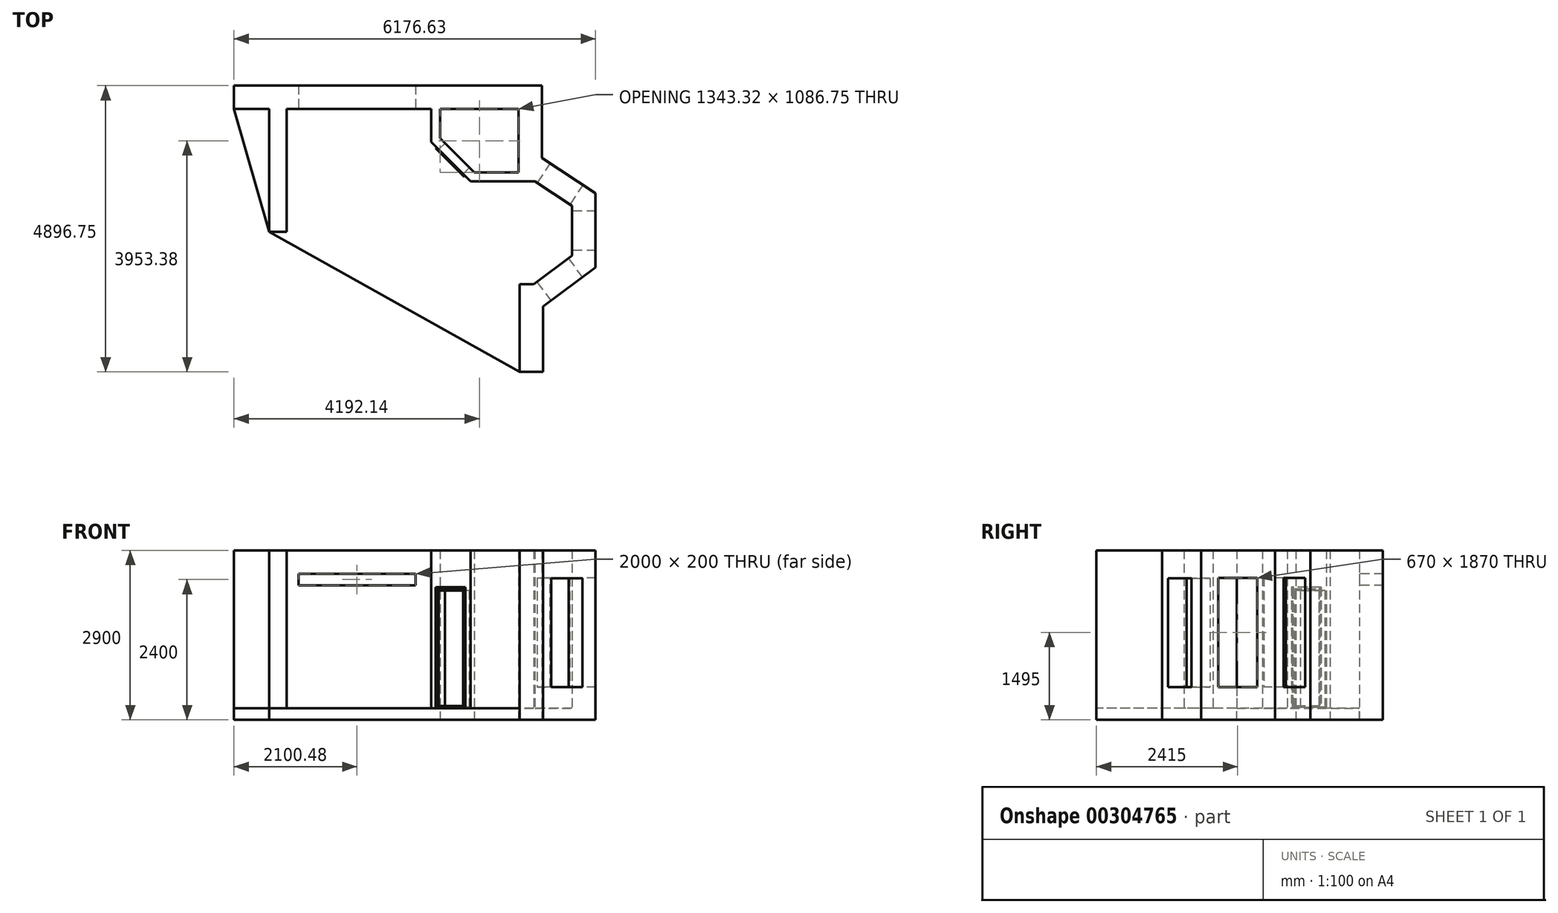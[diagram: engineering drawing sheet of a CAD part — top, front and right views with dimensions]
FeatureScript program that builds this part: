
annotation { "Feature Type Name" : "Feature", "Feature Type Description" : "" }
export const myFeature = defineFeature(function(context is Context, id is Id, definition is map)
    precondition{}
    {
        {
            var Q0;
            Q0=qCreatedBy(makeId("Top.planeOp"),FACE);
            var sketch = newSketch(context, id + "F0", { "sketchPlane" : qUnion([Q0])});
            skLineSegment(sketch, "E0", {"start": v(-112.53, -1087.53) * mm, "end": v(2357.47, -1087.53) * mm});
            skLineSegment(sketch, "E1", {"start": v(2357.47, -1087.53) * mm, "end": v(2357.47, -1652.53) * mm});
            skLineSegment(sketch, "E2", {"start": v(2357.47, -1652.53) * mm, "end": v(3029.22, -2324.28) * mm});
            skLineSegment(sketch, "E3", {"start": v(3029.22, -2324.28) * mm, "end": v(4130.22, -2324.28) * mm});
            skLineSegment(sketch, "E4", {"start": v(4130.22, -2324.28) * mm, "end": v(4763.62, -2744.28) * mm});
            skLineSegment(sketch, "E5", {"start": v(4763.62, -2744.28) * mm, "end": v(4763.62, -3594.28) * mm});
            skLineSegment(sketch, "E6", {"start": v(4763.62, -3594.28) * mm, "end": v(4106.13, -4084.28) * mm});
            skLineSegment(sketch, "E7", {"start": v(4106.13, -4084.28) * mm, "end": v(3866.13, -4084.28) * mm});
            skLineSegment(sketch, "E8", {"start": v(3866.13, -4084.28) * mm, "end": v(3866.13, -5584.28) * mm});
            skLineSegment(sketch, "E9", {"start": v(-112.53, -1087.53) * mm, "end": v(-112.53, -3187.53) * mm});
            skLineSegment(sketch, "E10", {"start": v(-112.53, -3187.53) * mm, "end": v(-412.53, -3187.53) * mm});
            skLineSegment(sketch, "E11", {"start": v(-412.53, -3187.53) * mm, "end": v(-412.53, -1087.53) * mm});
            skLineSegment(sketch, "E12", {"start": v(-412.53, -1087.53) * mm, "end": v(-1013, -1087.53) * mm});
            skLineSegment(sketch, "E13.0", {"start": v(4266.13, -4463.9) * mm, "end": v(4266.13, -5584.28) * mm});
            skLineSegment(sketch, "E13.1", {"start": v(5163.62, -3795.04) * mm, "end": v(4266.13, -4463.9) * mm});
            skLineSegment(sketch, "E13.2", {"start": v(5163.62, -2529.56) * mm, "end": v(5163.62, -3795.04) * mm});
            skLineSegment(sketch, "E13.3", {"start": v(4250.79, -1924.28) * mm, "end": v(5163.62, -2529.56) * mm});
            skLineSegment(sketch, "E13.4", {"start": v(-114.02, -687.53) * mm, "end": v(2757.47, -687.53) * mm});
            skLineSegment(sketch, "E13.5", {"start": v(2757.47, -687.53) * mm, "end": v(2757.47, -1486.84) * mm});
            skLineSegment(sketch, "E13.6", {"start": v(2757.47, -1486.84) * mm, "end": v(3194.9, -1924.28) * mm});
            skLineSegment(sketch, "E13.7", {"start": v(3194.9, -1924.28) * mm, "end": v(4250.79, -1924.28) * mm});
            skLineSegment(sketch, "E14", {"start": v(-1013, -1087.53) * mm, "end": v(-1013, -687.53) * mm});
            skLineSegment(sketch, "E15", {"start": v(-1013, -687.53) * mm, "end": v(-114.02, -687.53) * mm});
            skLineSegment(sketch, "E16", {"start": v(3866.13, -5584.28) * mm, "end": v(4266.13, -5584.28) * mm});
            skSolve(sketch);
        }
        {
            var Q0;
            Q0=makeQuery(id+"F0.imprint","IMPRINT",FACE,{"disambiguationData":[TD([[makeQuery(id+"F0.imprint","IMPRINT",EDGE,{"derivedFrom":sQuery(id+"F0.wireOp",EDGE,"E0")}),1.0]])]});
            extrude(context, id + "F1", {"entities" : qUnion([Q0]), "depth" : 2700 * mm});
        }
        {
            var Q0;
            Q0=qCreatedBy(makeId("Top.planeOp"),FACE);
            var sketch = newSketch(context, id + "F2", { "sketchPlane" : qUnion([Q0])});
            skPoint(sketch, "E17.0", {"position": v(3866.13, -4084.28) * mm});
            skLineSegment(sketch, "E18.0", {"start": v(3850.79, -1924.28) * mm, "end": v(4250.79, -1924.28) * mm});
            skLineSegment(sketch, "E19.0", {"start": v(2757.47, -687.53) * mm, "end": v(2757.47, -1087.53) * mm});
            skPoint(sketch, "E20.0", {"position": v(2357.47, -1087.53) * mm});
            skLineSegment(sketch, "E21", {"start": v(2757.47, -1087.53) * mm, "end": v(3850.79, -1087.53) * mm});
            skPoint(sketch, "E22.0", {"position": v(4266.13, -4463.9) * mm});
            skLineSegment(sketch, "E23", {"start": v(2757.47, -687.53) * mm, "end": v(4250.79, -687.53) * mm});
            skLineSegment(sketch, "E24", {"start": v(4250.79, -1924.28) * mm, "end": v(4250.79, -687.53) * mm});
            skLineSegment(sketch, "E25", {"start": v(3850.79, -1087.53) * mm, "end": v(3850.79, -1924.28) * mm});
            skPoint(sketch, "E26.orphan", {"position": v(3194.9, -1924.28) * mm});
            skPoint(sketch, "E27.orphan", {"position": v(2757.47, -1486.84) * mm});
            skSolve(sketch);
        }
        {
            var Q0;
            Q0=makeQuery(id+"F2.imprint","IMPRINT",FACE,{"disambiguationData":[TD([[makeQuery(id+"F2.imprint","IMPRINT",EDGE,{"derivedFrom":sQuery(id+"F2.wireOp",EDGE,"E18.0")}),1.0]])]});
            extrude(context, id + "F3", {"entities" : qUnion([Q0]), "operationType" : NewBodyOperationType.ADD, "depth" : 2700 * mm});
        }
        {
            var Q0;
            Q0=qCreatedBy(makeId("Top.planeOp"),FACE);
            var sketch = newSketch(context, id + "F4", { "sketchPlane" : qUnion([Q0])});
            skLineSegment(sketch, "E28.0", {"start": v(2757.47, -1087.53) * mm, "end": v(2757.47, -1486.84) * mm});
            skLineSegment(sketch, "E29.0", {"start": v(2757.47, -1486.84) * mm, "end": v(3194.9, -1924.28) * mm});
            skLineSegment(sketch, "E30.0", {"start": v(3194.9, -1924.28) * mm, "end": v(3850.79, -1924.28) * mm});
            skLineSegment(sketch, "E31", {"start": v(2757.47, -1087.53) * mm, "end": v(2507.47, -1087.53) * mm});
            skLineSegment(sketch, "E32", {"start": v(2507.47, -1087.53) * mm, "end": v(2507.47, -1590.4) * mm});
            skLineSegment(sketch, "E33", {"start": v(2507.47, -1590.4) * mm, "end": v(3091.35, -2174.28) * mm});
            skLineSegment(sketch, "E34", {"start": v(3091.35, -2174.28) * mm, "end": v(3850.79, -2174.28) * mm});
            skLineSegment(sketch, "E35", {"start": v(3850.79, -2174.28) * mm, "end": v(3850.79, -1924.28) * mm});
            skSolve(sketch);
        }
        {
            var Q0;
            Q0=makeQuery(id+"F4.imprint","IMPRINT",FACE,{"disambiguationData":[TD([[makeQuery(id+"F4.imprint","IMPRINT",EDGE,{"derivedFrom":sQuery(id+"F4.wireOp",EDGE,"E28.0")}),-1.0]])]});
            extrude(context, id + "F5", {"entities" : qUnion([Q0]), "operationType" : NewBodyOperationType.REMOVE, "depth" : 2700 * mm});
        }
        {
            var Q0;
            Q0=makeQuery(id+"F3.boolean.opBoolean","MERGE",FACE,{"derivedFrom":[makeQuery(id+"F1.opExtrude","CAP_FACE",FACE,{"disambiguationData":[OSD([sQuery(id+"F0.wireOp",EDGE,"E0"),sQuery(id+"F0.wireOp",EDGE,"E1"),sQuery(id+"F0.wireOp",EDGE,"E2"),sQuery(id+"F0.wireOp",EDGE,"E3"),sQuery(id+"F0.wireOp",EDGE,"E4"),sQuery(id+"F0.wireOp",EDGE,"E5"),sQuery(id+"F0.wireOp",EDGE,"E6"),sQuery(id+"F0.wireOp",EDGE,"E7"),sQuery(id+"F0.wireOp",EDGE,"E8"),sQuery(id+"F0.wireOp",EDGE,"E9"),sQuery(id+"F0.wireOp",EDGE,"E10"),sQuery(id+"F0.wireOp",EDGE,"E11"),sQuery(id+"F0.wireOp",EDGE,"E12"),sQuery(id+"F0.wireOp",EDGE,"E13.0"),sQuery(id+"F0.wireOp",EDGE,"E13.1"),sQuery(id+"F0.wireOp",EDGE,"E13.2"),sQuery(id+"F0.wireOp",EDGE,"E13.3"),sQuery(id+"F0.wireOp",EDGE,"E13.4"),sQuery(id+"F0.wireOp",EDGE,"E13.5"),sQuery(id+"F0.wireOp",EDGE,"E13.6"),sQuery(id+"F0.wireOp",EDGE,"E13.7"),sQuery(id+"F0.wireOp",EDGE,"E14"),sQuery(id+"F0.wireOp",EDGE,"E15"),sQuery(id+"F0.wireOp",EDGE,"E16")])],"isStart":true}),makeQuery(id+"F3.opExtrude","CAP_FACE",FACE,{"disambiguationData":[OSD([sQuery(id+"F2.wireOp",EDGE,"E18.0"),sQuery(id+"F2.wireOp",EDGE,"E19.0"),sQuery(id+"F2.wireOp",EDGE,"E21"),sQuery(id+"F2.wireOp",EDGE,"E23"),sQuery(id+"F2.wireOp",EDGE,"E24"),sQuery(id+"F2.wireOp",EDGE,"E25")])],"isStart":true})]});
            var sketch = newSketch(context, id + "F6", { "sketchPlane" : qUnion([Q0])});
            skLineSegment(sketch, "E36.0", {"start": v(-1013, 687.53) * mm, "end": v(4250.79, 687.53) * mm});
            skPoint(sketch, "E37.0", {"position": v(4250.79, 1305.9) * mm});
            skLineSegment(sketch, "E38.0", {"start": v(4250.79, 1924.28) * mm, "end": v(4250.79, 687.53) * mm});
            skLineSegment(sketch, "E39.0", {"start": v(4250.79, 1924.28) * mm, "end": v(5163.62, 2529.56) * mm});
            skPoint(sketch, "E40.0", {"position": v(5163.62, 3162.3) * mm});
            skLineSegment(sketch, "E41.0", {"start": v(5163.62, 2529.56) * mm, "end": v(5163.62, 3795.04) * mm});
            skLineSegment(sketch, "E42.0", {"start": v(5163.62, 3795.04) * mm, "end": v(4266.13, 4463.9) * mm});
            skLineSegment(sketch, "E43.0", {"start": v(4266.13, 4463.9) * mm, "end": v(4266.13, 5584.28) * mm});
            skLineSegment(sketch, "E44.0", {"start": v(-1013, 1087.53) * mm, "end": v(-1013, 687.53) * mm});
            skPoint(sketch, "E45.0", {"position": v(-412.53, 3187.53) * mm});
            skLineSegment(sketch, "E46.0", {"start": v(3866.13, 5584.28) * mm, "end": v(4266.13, 5584.28) * mm});
            skLineSegment(sketch, "E47", {"start": v(-1013, 1087.53) * mm, "end": v(-412.53, 3187.53) * mm});
            skLineSegment(sketch, "E48", {"start": v(-412.53, 3187.53) * mm, "end": v(3866.13, 5584.28) * mm});
            skSolve(sketch);
        }
        {
            var Q0;
            Q0=makeQuery(id+"F6.imprint","IMPRINT",FACE,{"disambiguationData":[TD([[makeQuery(id+"F6.imprint","IMPRINT",EDGE,{"derivedFrom":sQuery(id+"F6.wireOp",EDGE,"E36.0")}),1.0]])]});
            var Q1;
            Q1=makeQuery(id+"F6.imprint","IMPRINT",FACE,{"disambiguationData":[TD([[makeQuery(id+"F6.imprint","IMPRINT",EDGE,{"derivedFrom":sQuery(id+"F6.wireOp",EDGE,"E47")}),-1.0]])]});
            var Q2;
            Q2=makeQuery(id+"F6.imprint","IMPRINT",FACE,{"disambiguationData":[TD([[makeQuery(id+"F6.imprint","IMPRINT",EDGE,{"derivedFrom":sQuery(id+"F6.wireOp",EDGE,"E48")}),-1.0]])]});
            var Q3;
            Q3=makeQuery(id+"F6.imprint","IMPRINT",FACE,{"disambiguationData":[TD([[makeQuery(id+"F6.imprint","IMPRINT",EDGE,{"derivedFrom":makeQuery(id+"F5.boolean.opBoolean","COPY",EDGE,{"derivedFrom":makeQuery(id+"F5.opExtrude","CAP_EDGE",EDGE,{"disambiguationData":[OSD([sQuery(id+"F4.wireOp",EDGE,"E32")])],"isStart":true})})}),-1.0]])]});
            extrude(context, id + "F7", {"entities" : qUnion([Q0, Q1, Q2, Q3]), "operationType" : NewBodyOperationType.ADD, "depth" : 200 * mm});
        }
        {
            var Q0;
            Q0=makeQuery(id+"F1.opExtrude","SWEPT_FACE",FACE,{"disambiguationData":[OSD([sQuery(id+"F0.wireOp",EDGE,"E2")])]});
            var sketch = newSketch(context, id + "F8", { "sketchPlane" : qUnion([Q0])});
            skLineSegment(sketch, "E49.bottom", {"start": v(2965.5, 2070) * mm, "end": v(3655.5, 2070) * mm});
            skLineSegment(sketch, "E49.top", {"start": v(2965.5, 10) * mm, "end": v(3655.5, 10) * mm});
            skLineSegment(sketch, "E49.left", {"start": v(2965.5, 2070) * mm, "end": v(2965.5, 10) * mm});
            skLineSegment(sketch, "E49.right", {"start": v(3655.5, 2070) * mm, "end": v(3655.5, 10) * mm});
            skSolve(sketch);
        }
        {
            var Q0;
            Q0=makeQuery(id+"F8.imprint","IMPRINT",FACE,{"disambiguationData":[TD([[makeQuery(id+"F8.imprint","IMPRINT",EDGE,{"derivedFrom":sQuery(id+"F8.wireOp",EDGE,"E49.bottom")}),-1.0]])]});
            extrude(context, id + "F9", {"entities" : qUnion([Q0]), "operationType" : NewBodyOperationType.ADD, "depth" : 25 * mm});
        }
        {
            var Q0;
            Q0=makeQuery(id+"F1.opExtrude","SWEPT_FACE",FACE,{"disambiguationData":[OSD([sQuery(id+"F0.wireOp",EDGE,"E4")])]});
            var sketch = newSketch(context, id + "F10", { "sketchPlane" : qUnion([Q0])});
            skLineSegment(sketch, "E50.bottom", {"start": v(4771.7, 2230) * mm, "end": v(5441.7, 2230) * mm});
            skLineSegment(sketch, "E50.top", {"start": v(4771.7, 360) * mm, "end": v(5441.7, 360) * mm});
            skLineSegment(sketch, "E50.left", {"start": v(4771.7, 2230) * mm, "end": v(4771.7, 360) * mm});
            skLineSegment(sketch, "E50.right", {"start": v(5441.7, 2230) * mm, "end": v(5441.7, 360) * mm});
            skPoint(sketch, "E51.0", {"position": v(5106.7, 2700) * mm});
            skSolve(sketch);
        }
        {
            var Q0;
            Q0=makeQuery(id+"F10.imprint","IMPRINT",FACE,{"disambiguationData":[TD([[makeQuery(id+"F10.imprint","IMPRINT",EDGE,{"derivedFrom":sQuery(id+"F10.wireOp",EDGE,"E50.bottom")}),-1.0]])]});
            extrude(context, id + "F11", {"entities" : qUnion([Q0]), "operationType" : NewBodyOperationType.REMOVE, "oppositeDirection" : true, "depth" : 500 * mm});
        }
        {
            var Q0;
            Q0=makeQuery(id+"F1.opExtrude","SWEPT_FACE",FACE,{"disambiguationData":[OSD([sQuery(id+"F0.wireOp",EDGE,"E5")])]});
            var sketch = newSketch(context, id + "F12", { "sketchPlane" : qUnion([Q0])});
            skLineSegment(sketch, "E52.bottom", {"start": v(2834.28, 2230) * mm, "end": v(3504.28, 2230) * mm});
            skLineSegment(sketch, "E52.top", {"start": v(2834.28, 360) * mm, "end": v(3504.28, 360) * mm});
            skLineSegment(sketch, "E52.left", {"start": v(2834.28, 2230) * mm, "end": v(2834.28, 360) * mm});
            skLineSegment(sketch, "E52.right", {"start": v(3504.28, 2230) * mm, "end": v(3504.28, 360) * mm});
            skPoint(sketch, "E53.0", {"position": v(3169.28, 2700) * mm});
            skSolve(sketch);
        }
        {
            var Q0;
            Q0=makeQuery(id+"F12.imprint","IMPRINT",FACE,{"disambiguationData":[TD([[makeQuery(id+"F12.imprint","IMPRINT",EDGE,{"derivedFrom":sQuery(id+"F12.wireOp",EDGE,"E52.bottom")}),-1.0]])]});
            extrude(context, id + "F13", {"entities" : qUnion([Q0]), "operationType" : NewBodyOperationType.REMOVE, "oppositeDirection" : true, "depth" : 500 * mm});
        }
        {
            var Q0;
            Q0=makeQuery(id+"F1.opExtrude","SWEPT_FACE",FACE,{"disambiguationData":[OSD([sQuery(id+"F0.wireOp",EDGE,"E6")])]});
            var sketch = newSketch(context, id + "F14", { "sketchPlane" : qUnion([Q0])});
            skLineSegment(sketch, "E54.bottom", {"start": v(-1596.79, 2220) * mm, "end": v(-926.79, 2220) * mm});
            skLineSegment(sketch, "E54.top", {"start": v(-1596.79, 360) * mm, "end": v(-926.79, 360) * mm});
            skLineSegment(sketch, "E54.left", {"start": v(-1596.79, 2220) * mm, "end": v(-1596.79, 360) * mm});
            skLineSegment(sketch, "E54.right", {"start": v(-926.79, 2220) * mm, "end": v(-926.79, 360) * mm});
            skPoint(sketch, "E55.0", {"position": v(-1261.79, 2700) * mm});
            skSolve(sketch);
        }
        {
            var Q0;
            Q0 = qSketchRegion(id + "F14", true);
            extrude(context, id + "F15", {"entities" : qUnion([Q0]), "operationType" : NewBodyOperationType.REMOVE, "oppositeDirection" : true, "depth" : 500 * mm});
        }
        {
            var Q0;
            Q0=makeQuery(id+"F1.opExtrude","SWEPT_FACE",FACE,{"disambiguationData":[OSD([sQuery(id+"F0.wireOp",EDGE,"E0")])]});
            var sketch = newSketch(context, id + "F16", { "sketchPlane" : qUnion([Q0])});
            skLineSegment(sketch, "E56.bottom", {"start": v(87.47, 2300) * mm, "end": v(2087.47, 2300) * mm});
            skLineSegment(sketch, "E56.top", {"start": v(87.47, 2100) * mm, "end": v(2087.47, 2100) * mm});
            skLineSegment(sketch, "E56.left", {"start": v(87.47, 2300) * mm, "end": v(87.47, 2100) * mm});
            skLineSegment(sketch, "E56.right", {"start": v(2087.47, 2300) * mm, "end": v(2087.47, 2100) * mm});
            skSolve(sketch);
        }
        {
            var Q0;
            Q0=makeQuery(id+"F16.imprint","IMPRINT",FACE,{"disambiguationData":[TD([[makeQuery(id+"F16.imprint","IMPRINT",EDGE,{"derivedFrom":sQuery(id+"F16.wireOp",EDGE,"E56.bottom")}),-1.0]])]});
            extrude(context, id + "F17", {"entities" : qUnion([Q0]), "operationType" : NewBodyOperationType.REMOVE, "oppositeDirection" : true, "depth" : 500 * mm});
        }
        {
            var Q0;
            {var subQ0=sQuery(id+"F6.wireOp",EDGE,"E46.0");var subQ1=sQuery(id+"F6.wireOp",EDGE,"E48");var subQ2=sQuery(id+"F6.wireOp",EDGE,"E47");var subQ3=makeQuery(id+"F7.opExtrude","CAP_FACE",FACE,{"disambiguationData":[OSD([sQuery(id+"F6.wireOp",EDGE,"E36.0"),sQuery(id+"F6.wireOp",EDGE,"E38.0"),sQuery(id+"F6.wireOp",EDGE,"E39.0"),sQuery(id+"F6.wireOp",EDGE,"E41.0"),sQuery(id+"F6.wireOp",EDGE,"E42.0"),sQuery(id+"F6.wireOp",EDGE,"E43.0"),sQuery(id+"F6.wireOp",EDGE,"E44.0"),subQ0,subQ2,subQ1])],"isStart":true});Q0=makeQuery(id+"F7.boolean.opBoolean","SPLIT",FACE,{"disambiguationData":[TD([makeQuery(id+"F1.opExtrude","SWEPT_FACE",FACE,{"disambiguationData":[OSD([sQuery(id+"F0.wireOp",EDGE,"E0")])]})])],"derivedFrom":subQ3});}
            var sketch = newSketch(context, id + "F18", { "sketchPlane" : qUnion([Q0])});
            skPoint(sketch, "E57.0", {"position": v(-112.53, -1087.53) * mm});
            skLineSegment(sketch, "E58.0", {"start": v(-112.53, -1087.53) * mm, "end": v(-112.53, -3187.53) * mm});
            skLineSegment(sketch, "E59.0", {"start": v(-112.53, -1087.53) * mm, "end": v(2357.47, -1087.53) * mm});
            skLineSegment(sketch, "E60", {"start": v(-112.53, -3187.53) * mm, "end": v(487.47, -3187.53) * mm});
            skLineSegment(sketch, "E61", {"start": v(487.47, -3187.53) * mm, "end": v(487.47, -2111.8) * mm});
            skLineSegment(sketch, "E62", {"start": v(487.47, -2111.8) * mm, "end": v(911.73, -1687.53) * mm});
            skLineSegment(sketch, "E63", {"start": v(911.73, -1687.53) * mm, "end": v(1797.47, -1687.53) * mm});
            skLineSegment(sketch, "E64", {"start": v(1797.47, -1687.53) * mm, "end": v(1797.47, -1087.53) * mm});
            skSolve(sketch);
        }
        {
            var Q0;
            Q0=makeQuery(id+"F8.imprint","IMPRINT",FACE,{"disambiguationData":[TD([[makeQuery(id+"F8.imprint","IMPRINT",EDGE,{"derivedFrom":sQuery(id+"F8.wireOp",EDGE,"E49.bottom")}),-1.0]])]});
            var sketch = newSketch(context, id + "F19", { "sketchPlane" : qUnion([Q0])});
            skLineSegment(sketch, "E65.bottom", {"start": v(3015.5, 2010) * mm, "end": v(3605.5, 2010) * mm});
            skLineSegment(sketch, "E65.top", {"start": v(3015.5, 20) * mm, "end": v(3605.5, 20) * mm});
            skLineSegment(sketch, "E65.left", {"start": v(3015.5, 2010) * mm, "end": v(3015.5, 20) * mm});
            skLineSegment(sketch, "E65.right", {"start": v(3605.5, 2010) * mm, "end": v(3605.5, 20) * mm});
            skPoint(sketch, "E65.middle", {"position": v(3310.5, 1015) * mm});
            skSolve(sketch);
        }
        {
            var Q0;
            Q0=makeQuery(id+"F19.imprint","IMPRINT",FACE,{"disambiguationData":[TD([[makeQuery(id+"F19.imprint","IMPRINT",EDGE,{"derivedFrom":sQuery(id+"F19.wireOp",EDGE,"E65.bottom")}),-1.0]])]});
            extrude(context, id + "F20", {"entities" : qUnion([Q0]), "operationType" : NewBodyOperationType.REMOVE, "oppositeDirection" : true, "depth" : 300 * mm});
        }
        {
            var Q0;
            Q0=makeQuery(id+"F9.opExtrude","CAP_FACE",FACE,{"disambiguationData":[OSD([sQuery(id+"F8.wireOp",EDGE,"E49.bottom"),sQuery(id+"F8.wireOp",EDGE,"E49.top"),sQuery(id+"F8.wireOp",EDGE,"E49.left"),sQuery(id+"F8.wireOp",EDGE,"E49.right")])],"isStart":false});
            var sketch = newSketch(context, id + "F21", { "sketchPlane" : qUnion([Q0])});
            skLineSegment(sketch, "E66.0.0", {"start": v(2965.5, 2070) * mm, "end": v(2965.5, 10) * mm});
            skLineSegment(sketch, "E66.0.1", {"start": v(2965.5, 10) * mm, "end": v(3655.5, 10) * mm});
            skLineSegment(sketch, "E66.0.2", {"start": v(3655.5, 10) * mm, "end": v(3655.5, 2070) * mm});
            skLineSegment(sketch, "E66.0.3", {"start": v(3655.5, 2070) * mm, "end": v(2965.5, 2070) * mm});
            skLineSegment(sketch, "E67.0", {"start": v(2990.5, 2045) * mm, "end": v(2990.5, 35) * mm});
            skLineSegment(sketch, "E67.1", {"start": v(3630.5, 2045) * mm, "end": v(2990.5, 2045) * mm});
            skLineSegment(sketch, "E67.2", {"start": v(3630.5, 35) * mm, "end": v(3630.5, 2045) * mm});
            skLineSegment(sketch, "E67.3", {"start": v(2990.5, 35) * mm, "end": v(3630.5, 35) * mm});
            skLineSegment(sketch, "E68.0", {"start": v(2960.5, 2075) * mm, "end": v(2960.5, 5) * mm});
            skLineSegment(sketch, "E68.1", {"start": v(3660.5, 2075) * mm, "end": v(2960.5, 2075) * mm});
            skLineSegment(sketch, "E68.2", {"start": v(3660.5, 5) * mm, "end": v(3660.5, 2075) * mm});
            skLineSegment(sketch, "E68.3", {"start": v(2960.5, 5) * mm, "end": v(3660.5, 5) * mm});
            skSolve(sketch);
        }
        {
            var Q0;
            Q0=makeQuery(id+"F21.imprint","IMPRINT",FACE,{"disambiguationData":[TD([[makeQuery(id+"F21.imprint","IMPRINT",EDGE,{"derivedFrom":sQuery(id+"F21.wireOp",EDGE,"E67.0")}),1.0]])]});
            extrude(context, id + "F22", {"entities" : qUnion([Q0]), "operationType" : NewBodyOperationType.REMOVE, "oppositeDirection" : true, "depth" : 25 * mm});
        }
    });
